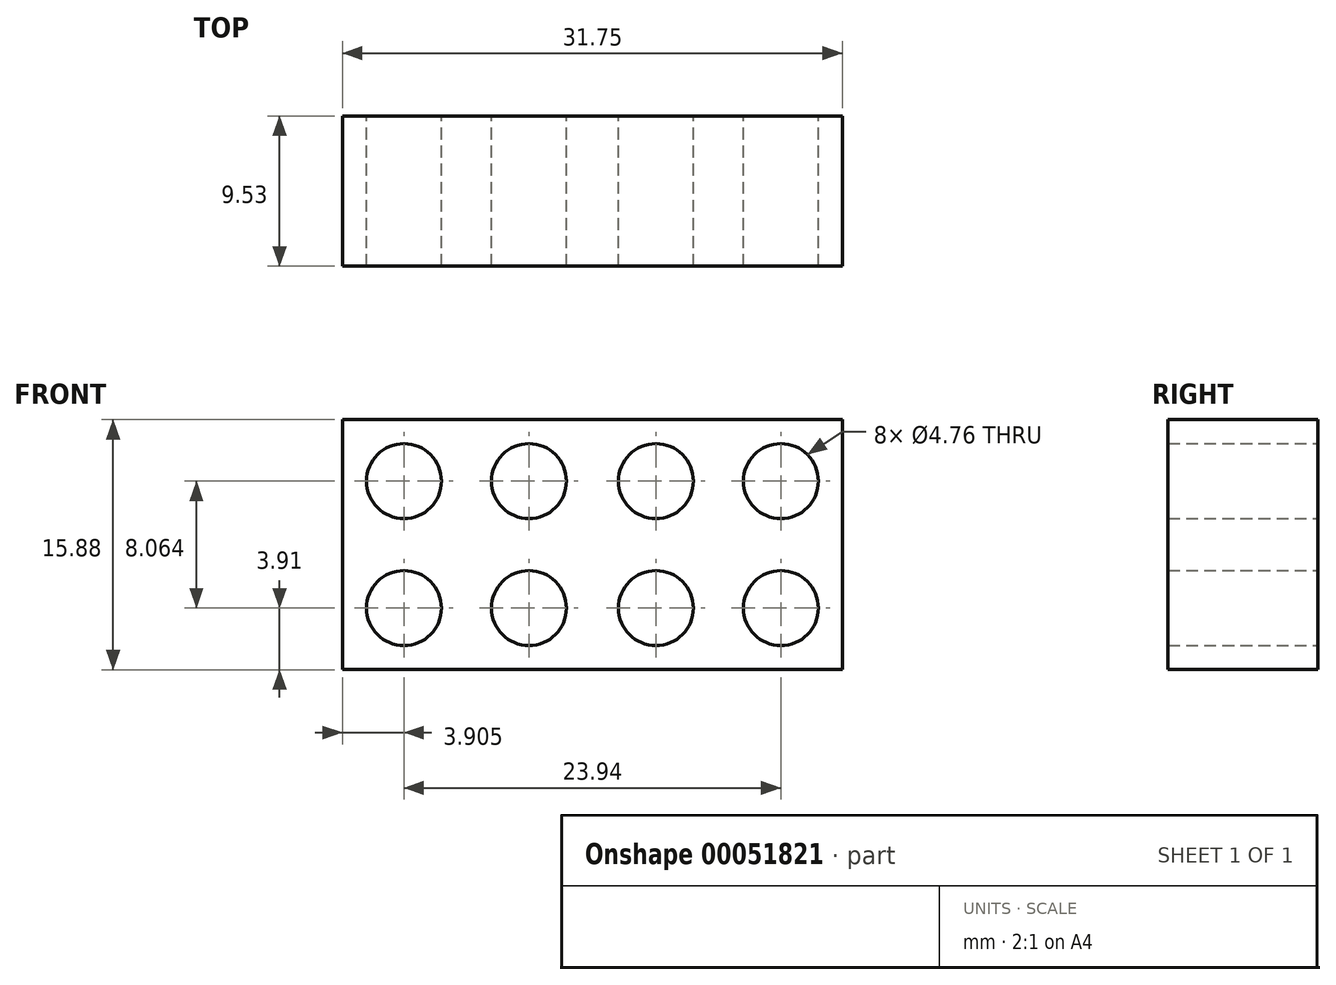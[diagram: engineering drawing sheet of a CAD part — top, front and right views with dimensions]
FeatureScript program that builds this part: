
annotation { "Feature Type Name" : "Feature", "Feature Type Description" : "" }
export const myFeature = defineFeature(function(context is Context, id is Id, definition is map)
    precondition{}
    {
        {
            var Q0;
            Q0=qCreatedBy(makeId("Front.planeOp"),FACE);
            var sketch = newSketch(context, id + "F0", { "sketchPlane" : qUnion([Q0])});
            skLineSegment(sketch, "E0.bottom", {"start": v(0, 0) * mm, "end": v(-31.75, 0) * mm});
            skLineSegment(sketch, "E0.top", {"start": v(0, -15.88) * mm, "end": v(-31.75, -15.88) * mm});
            skLineSegment(sketch, "E0.left", {"start": v(0, 0) * mm, "end": v(0, -15.88) * mm});
            skLineSegment(sketch, "E0.right", {"start": v(-31.75, 0) * mm, "end": v(-31.75, -15.88) * mm});
            skCircle(sketch, "E1", {"center": v(-27.84, -3.9) * mm, "radius": 2.38 * mm});
            skCircle(sketch, "E2.MirrorC", {"center": v(-19.9, -3.9) * mm, "radius": 2.38 * mm});
            skCircle(sketch, "E3.MirrorC", {"center": v(-27.84, -11.97) * mm, "radius": 2.38 * mm});
            skCircle(sketch, "E4.MirrorC", {"center": v(-19.9, -11.97) * mm, "radius": 2.38 * mm});
            skCircle(sketch, "E5.MirrorC", {"center": v(-11.84, -3.9) * mm, "radius": 2.38 * mm});
            skCircle(sketch, "E6.MirrorC", {"center": v(-3.9, -3.9) * mm, "radius": 2.38 * mm});
            skCircle(sketch, "E7.MirrorC", {"center": v(-3.9, -11.97) * mm, "radius": 2.38 * mm});
            skCircle(sketch, "E8.MirrorC", {"center": v(-11.84, -11.97) * mm, "radius": 2.38 * mm});
            skSolve(sketch);
        }
        {
            var Q0;
            Q0 = qSketchRegion(id + "F0", true);
            extrude(context, id + "F1", {"entities" : qUnion([Q0]), "depth" : 9.52 * mm});
        }
        {
            var Q0;
            Q0=sQuery(id+"F0.wireOp",EDGE,"E7.MirrorC");
            extrude(context, id + "F2", {"bodyType" : ToolBodyType.SURFACE, "surfaceEntities" : qUnion([Q0]), "oppositeDirection" : true, "depth" : 2.5 * mm});
        }
    });
